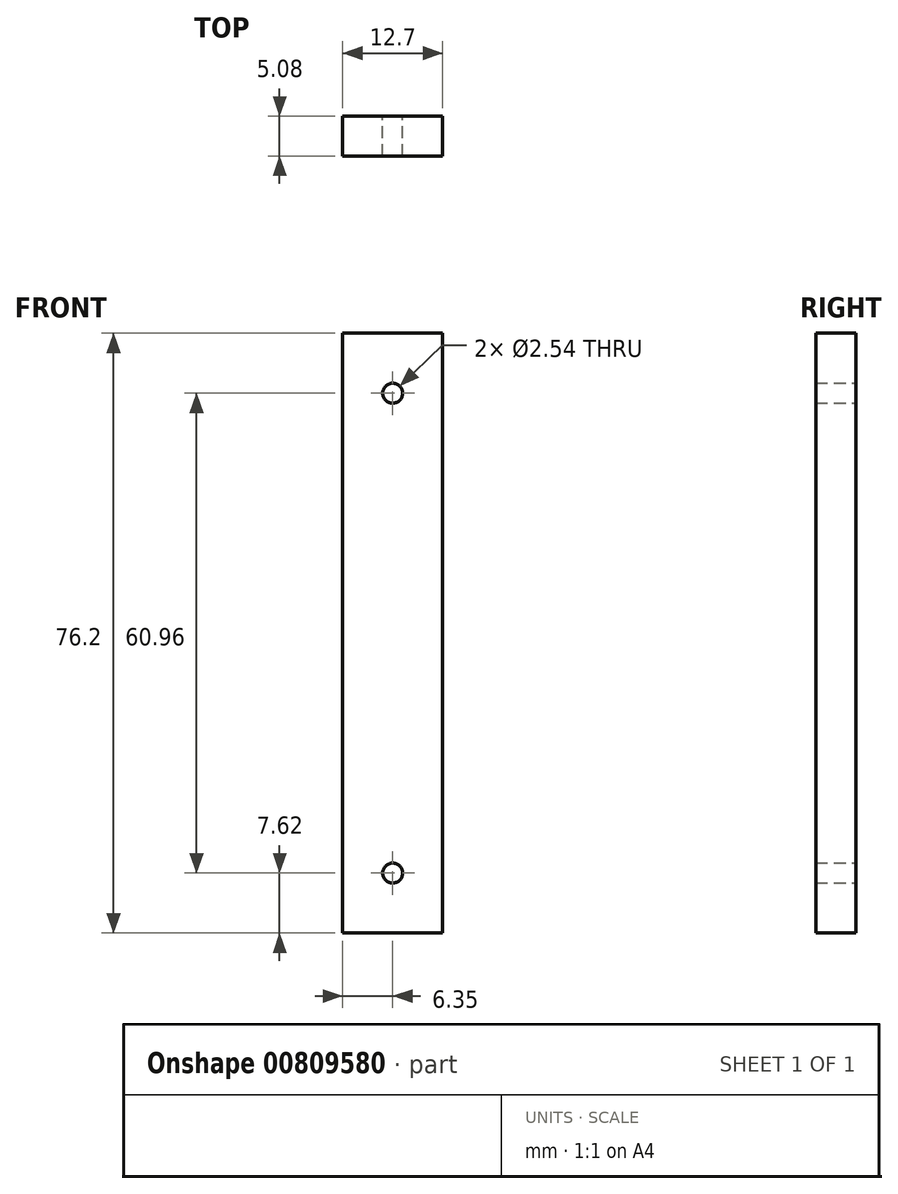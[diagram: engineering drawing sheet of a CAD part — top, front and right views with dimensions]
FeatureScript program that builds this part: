
annotation { "Feature Type Name" : "Feature", "Feature Type Description" : "" }
export const myFeature = defineFeature(function(context is Context, id is Id, definition is map)
    precondition{}
    {
        {
            var Q0;
            Q0=qCreatedBy(makeId("Front.planeOp"),FACE);
            var sketch = newSketch(context, id + "F0", { "sketchPlane" : qUnion([Q0])});
            skLineSegment(sketch, "E0.bottom", {"start": v(6.35, 38.1) * mm, "end": v(-6.35, 38.1) * mm});
            skLineSegment(sketch, "E0.top", {"start": v(6.35, -38.1) * mm, "end": v(-6.35, -38.1) * mm});
            skLineSegment(sketch, "E0.left", {"start": v(6.35, 38.1) * mm, "end": v(6.35, -38.1) * mm});
            skLineSegment(sketch, "E0.right", {"start": v(-6.35, 38.1) * mm, "end": v(-6.35, -38.1) * mm});
            skPoint(sketch, "E0.middle", {"position": v(0, 0) * mm});
            skCircle(sketch, "E1", {"center": v(0, 30.48) * mm, "radius": 1.27 * mm});
            skCircle(sketch, "E2", {"center": v(0, -30.48) * mm, "radius": 1.27 * mm});
            skSolve(sketch);
        }
        {
            var Q0;
            Q0 = qSketchRegion(id + "F0", true);
            extrude(context, id + "F1", {"entities" : qUnion([Q0]), "depth" : 5.08 * mm, "offsetDistance" : 25.4 * mm});
        }
    });
